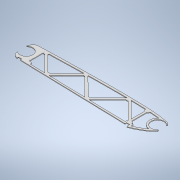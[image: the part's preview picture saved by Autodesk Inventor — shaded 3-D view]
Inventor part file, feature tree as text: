
AUTODESK INVENTOR PART (.ipt)
format: ipt  version: 2022 (Build 260153000, 153)  size: 382,464 bytes
history: native  units: mm
features: extrude x1, sketch x1
ambient origin geometry x8: Origin, YZ Plane, XZ Plane, XY Plane, X Axis, Y Axis, Z Axis, Center Point
bodies: Body1 (feature_tree)
feature tree (2):
  extrude  "Extrusion5"  Depth=10.0mm
  sketch  "Sketch1"  dims[d31=34.456mm d50=368.759386mm d57=16.0mm d69=8.0mm d70=23.0mm d71=8.0mm d73=16.0mm d80=19.0mm d81=16.0mm d82=1.0mm d83=1.0mm d84=1.0mm d85=1.0mm d86=1.0mm d87=0.8mm d88=1.0mm d90=19.0mm d94=5.0mm d95=5.0mm d105=5.0mm d106=5.0mm d108=2.0mm d109=19.0mm d114=5.0mm d115=5.0mm d116=24.0mm d117=2.5mm d118=2.5mm d123=2.5mm d124=2.5mm d125=10.0mm d126=24.0mm d127=24.0mm d128=27.0mm d135=0.5mm d136=45.0deg d139=7.0mm d165=45.0deg d169=27.0mm d175=90.0deg d181=45.0deg d185=7.0mm d186=45.0deg d190=7.0mm d191=45.0deg d197=90.0deg d203=90.0deg d206=7.0mm d207=1.0mm d208=0.0mm]
